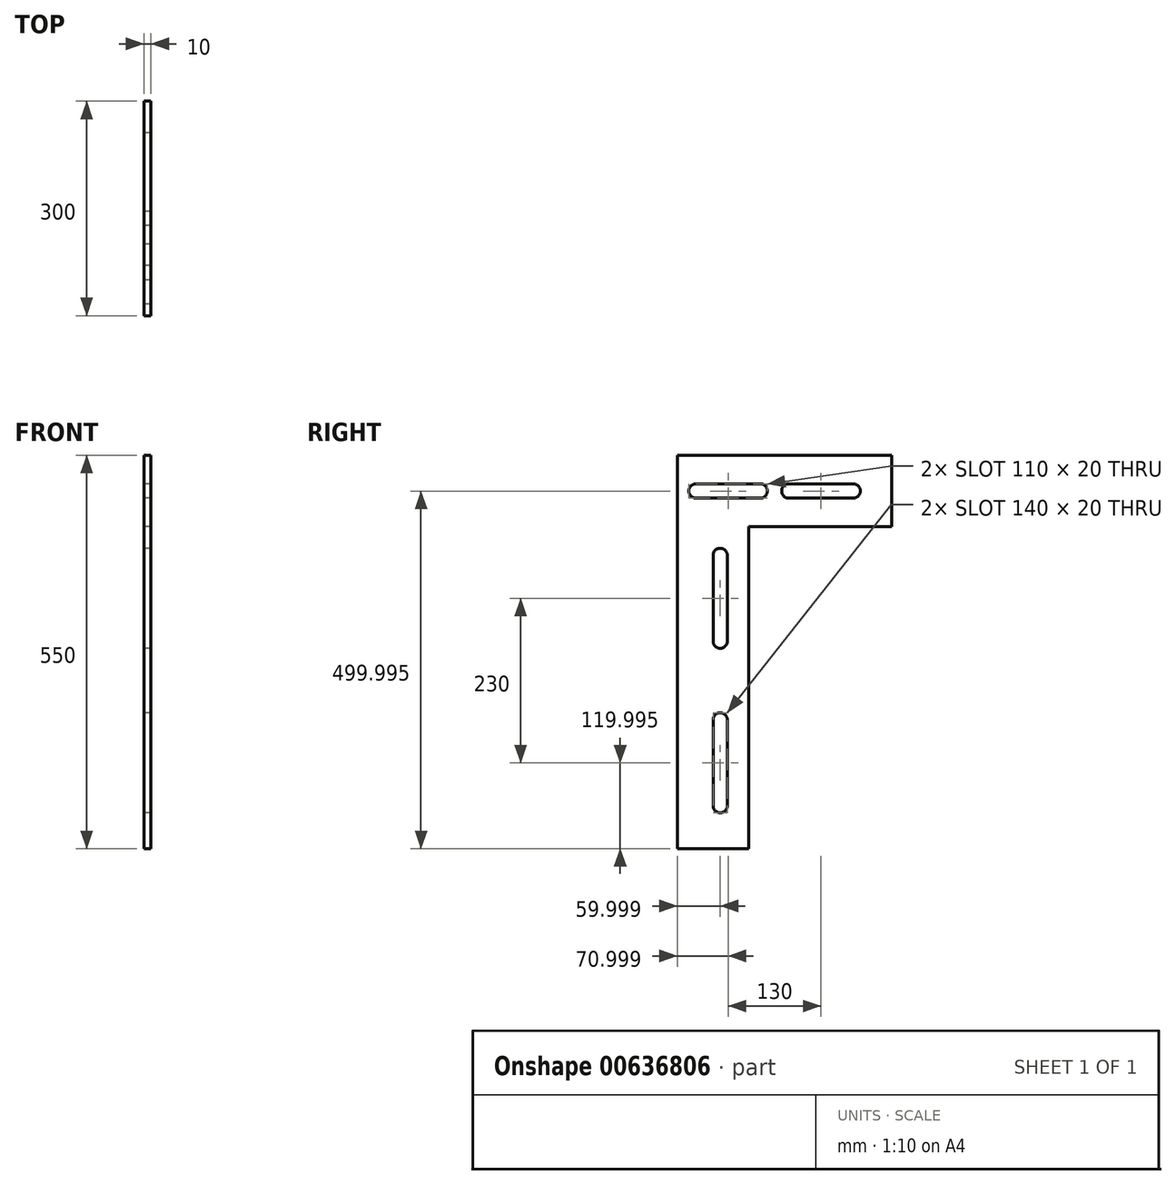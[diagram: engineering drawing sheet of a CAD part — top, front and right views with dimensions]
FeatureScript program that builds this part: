
annotation { "Feature Type Name" : "Feature", "Feature Type Description" : "" }
export const myFeature = defineFeature(function(context is Context, id is Id, definition is map)
    precondition{}
    {
        {
            var Q0;
            Q0=qCreatedBy(makeId("Right.planeOp"),FACE);
            var sketch = newSketch(context, id + "F0", { "sketchPlane" : qUnion([Q0])});
            skLineSegment(sketch, "E0.0", {"start": v(-109.38, -351.9) * mm, "end": v(-9.38, -351.9) * mm});
            skLineSegment(sketch, "E1.0", {"start": v(-109.38, 198.1) * mm, "end": v(-109.38, -351.9) * mm});
            skLineSegment(sketch, "E2.0", {"start": v(190.62, 198.1) * mm, "end": v(-109.38, 198.1) * mm});
            skLineSegment(sketch, "E3.0", {"start": v(190.62, 98.1) * mm, "end": v(190.62, 198.1) * mm});
            skLineSegment(sketch, "E4.0", {"start": v(-9.38, 98.1) * mm, "end": v(190.62, 98.1) * mm});
            skLineSegment(sketch, "E5.0", {"start": v(-9.38, -351.9) * mm, "end": v(-9.38, 98.1) * mm});
            skLineSegment(sketch, "E6.0", {"start": v(-59.38, -171.9) * mm, "end": v(-59.38, -291.9) * mm});
            skArc(sketch, "E7.0", {"start": v(-39.38, -171.9) * mm, "mid": v(-49.38, -161.9) * mm, "end": v(-59.38, -171.9) * mm});
            skLineSegment(sketch, "E8.0", {"start": v(-39.38, -291.9) * mm, "end": v(-39.38, -171.9) * mm});
            skArc(sketch, "E9.0", {"start": v(-59.38, -291.9) * mm, "mid": v(-49.38, -301.9) * mm, "end": v(-39.38, -291.9) * mm});
            skLineSegment(sketch, "E10.0", {"start": v(-39.38, -61.9) * mm, "end": v(-39.38, 58.1) * mm});
            skLineSegment(sketch, "E11.0", {"start": v(-59.38, 58.1) * mm, "end": v(-59.38, -61.9) * mm});
            skArc(sketch, "E12.0", {"start": v(-59.38, -61.9) * mm, "mid": v(-49.38, -71.9) * mm, "end": v(-39.38, -61.9) * mm});
            skArc(sketch, "E13.0", {"start": v(-39.38, 58.1) * mm, "mid": v(-49.38, 68.1) * mm, "end": v(-59.38, 58.1) * mm});
            skLineSegment(sketch, "E14.0", {"start": v(6.62, 158.1) * mm, "end": v(-83.38, 158.1) * mm});
            skArc(sketch, "E15.0", {"start": v(-83.38, 158.1) * mm, "mid": v(-93.38, 148.1) * mm, "end": v(-83.38, 138.1) * mm});
            skArc(sketch, "E16.0", {"start": v(6.62, 138.1) * mm, "mid": v(16.62, 148.1) * mm, "end": v(6.62, 158.1) * mm});
            skLineSegment(sketch, "E17.0", {"start": v(46.62, 138.1) * mm, "end": v(136.62, 138.1) * mm});
            skLineSegment(sketch, "E18.0", {"start": v(136.62, 158.1) * mm, "end": v(46.62, 158.1) * mm});
            skArc(sketch, "E19.0", {"start": v(136.62, 138.1) * mm, "mid": v(146.62, 148.1) * mm, "end": v(136.62, 158.1) * mm});
            skArc(sketch, "E20.0", {"start": v(46.62, 158.1) * mm, "mid": v(36.62, 148.1) * mm, "end": v(46.62, 138.1) * mm});
            skLineSegment(sketch, "E21", {"start": v(-83.38, 138.1) * mm, "end": v(6.62, 138.1) * mm});
            skSolve(sketch);
        }
        {
            var Q0;
            Q0=makeQuery(id+"F0.imprint","IMPRINT",FACE,{"disambiguationData":[TD([[makeQuery(id+"F0.imprint","IMPRINT",EDGE,{"derivedFrom":sQuery(id+"F0.wireOp",EDGE,"E0.0")}),1.0]])]});
            extrude(context, id + "F1", {"entities" : qUnion([Q0]), "depth" : 10 * mm, "offsetDistance" : 25 * mm});
        }
    });
